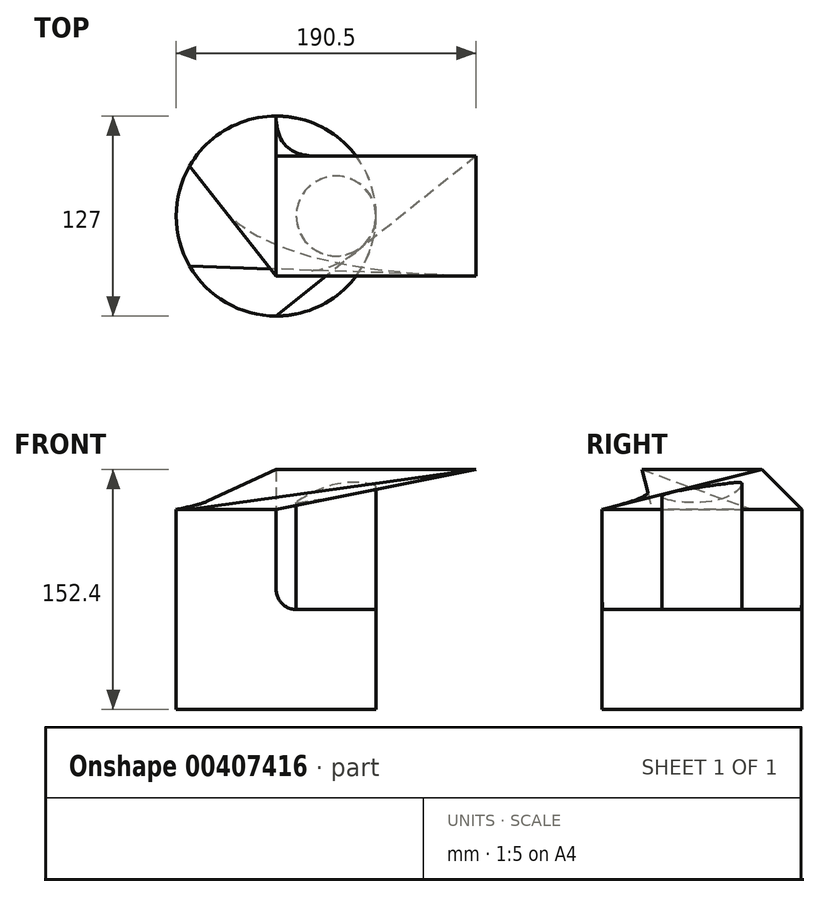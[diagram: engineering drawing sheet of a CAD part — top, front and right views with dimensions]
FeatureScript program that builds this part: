
annotation { "Feature Type Name" : "Feature", "Feature Type Description" : "" }
export const myFeature = defineFeature(function(context is Context, id is Id, definition is map)
    precondition{}
    {
        {
            var Q0;
            Q0=qCreatedBy(makeId("Top.planeOp"),FACE);
            var sketch = newSketch(context, id + "F0", { "sketchPlane" : qUnion([Q0])});
            skCircle(sketch, "E0", {"center": v(0, 0) * mm, "radius": 63.5 * mm});
            skSolve(sketch);
        }
        {
            var Q0;
            Q0 = qSketchRegion(id + "F0", true);
            extrude(context, id + "F1", {"entities" : qUnion([Q0]), "depth" : 127 * mm});
        }
        {
            var Q0;
            Q0=makeQuery(id+"F1.opExtrude","CAP_FACE",FACE,{"disambiguationData":[OSD([sQuery(id+"F0.wireOp",EDGE,"E0")])],"isStart":false});
            var sketch = newSketch(context, id + "F2", { "sketchPlane" : qUnion([Q0])});
            skLineSegment(sketch, "E1", {"start": v(0, -63.5) * mm, "end": v(0, 63.5) * mm});
            skLineSegment(sketch, "E2", {"start": v(0, 63.5) * mm, "end": v(63.5, 63.5) * mm});
            skLineSegment(sketch, "E3", {"start": v(63.5, 63.5) * mm, "end": v(63.5, -63.5) * mm});
            skLineSegment(sketch, "E4", {"start": v(63.5, -63.5) * mm, "end": v(0, -63.5) * mm});
            skSolve(sketch);
        }
        {
            var Q0;
            {var subQ0=sQuery(id+"F2.wireOp",EDGE,"E1");Q0=makeQuery(id+"F2.imprint","IMPRINT",FACE,{"disambiguationData":[TD([[makeQuery(id+"F2.imprint","IMPRINT",EDGE,{"derivedFrom":subQ0}),-1.0]])]});}
            extrude(context, id + "F3", {"entities" : qUnion([Q0]), "operationType" : NewBodyOperationType.REMOVE, "oppositeDirection" : true, "depth" : 63.5 * mm});
        }
        {
            var Q0;
            Q0=makeQuery(id+"F3.boolean.opBoolean","COPY",EDGE,{"derivedFrom":makeQuery(id+"F3.opExtrude","CAP_EDGE",EDGE,{"disambiguationData":[OSD([sQuery(id+"F2.wireOp",EDGE,"E1")])],"isStart":false})});
            fillet(context, id + "F4", {"entities" : qUnion([Q0]), "radius" : 12.7 * mm, "tangentPropagation" : true, "allowEdgeOverflow" : false});
        }
        {
            var Q0;
            Q0=qCreatedBy(makeId("Top.planeOp"),FACE);
            cPlane(context, id + "F5", {"entities" : qUnion([Q0]), "cplaneType" : CPlaneType.OFFSET, "offset" : 152.4 * mm, "width" : 152.4 * mm, "height" : 152.4 * mm});
        }
        {
            var Q0;
            Q0=qCreatedBy(id+"F5.planeOp",FACE);
            var sketch = newSketch(context, id + "F6", { "sketchPlane" : qUnion([Q0])});
            skCircle(sketch, "E5", {"center": v(38.1, 0) * mm, "radius": 25.4 * mm});
            skSolve(sketch);
        }
        {
            var Q0;
            Q0 = qSketchRegion(id + "F6", true);
            var Q1;
            Q1=makeQuery(id+"F3.boolean.opBoolean","COPY",FACE,{"derivedFrom":makeQuery(id+"F3.opExtrude","CAP_FACE",FACE,{"disambiguationData":[OSD([sQuery(id+"F0.wireOp",EDGE,"E0"),sQuery(id+"F2.wireOp",EDGE,"E1")])],"isStart":false})});
            extrude(context, id + "F7", {"entities" : qUnion([Q0]), "operationType" : NewBodyOperationType.ADD, "oppositeDirection" : true, "depth" : 99.57 * mm});
        }
        {
            var Q0;
            Q0=qCreatedBy(id+"F5.planeOp",FACE);
            var sketch = newSketch(context, id + "F8", { "sketchPlane" : qUnion([Q0])});
            skLineSegment(sketch, "E6.bottom", {"start": v(0, 38.1) * mm, "end": v(127, 38.1) * mm});
            skLineSegment(sketch, "E6.top", {"start": v(0, -38.1) * mm, "end": v(127, -38.1) * mm});
            skLineSegment(sketch, "E6.left", {"start": v(0, 38.1) * mm, "end": v(0, -38.1) * mm});
            skLineSegment(sketch, "E6.right", {"start": v(127, 38.1) * mm, "end": v(127, -38.1) * mm});
            skSolve(sketch);
        }
        {
            var Q1;
            Q1 = qSketchRegion(id + "F8", true);
            var Q2;
            Q2=makeQuery(id+"F1.opExtrude","CAP_FACE",FACE,{"disambiguationData":[OSD([sQuery(id+"F0.wireOp",EDGE,"E0")])],"isStart":false});
            loft(context, id + "F9", {"operationType" : NewBodyOperationType.ADD, "sheetProfilesArray" : [{ "sheetProfileEntities" : qUnion([Q1]) }, { "sheetProfileEntities" : qUnion([Q2]) }]});
        }
    });
